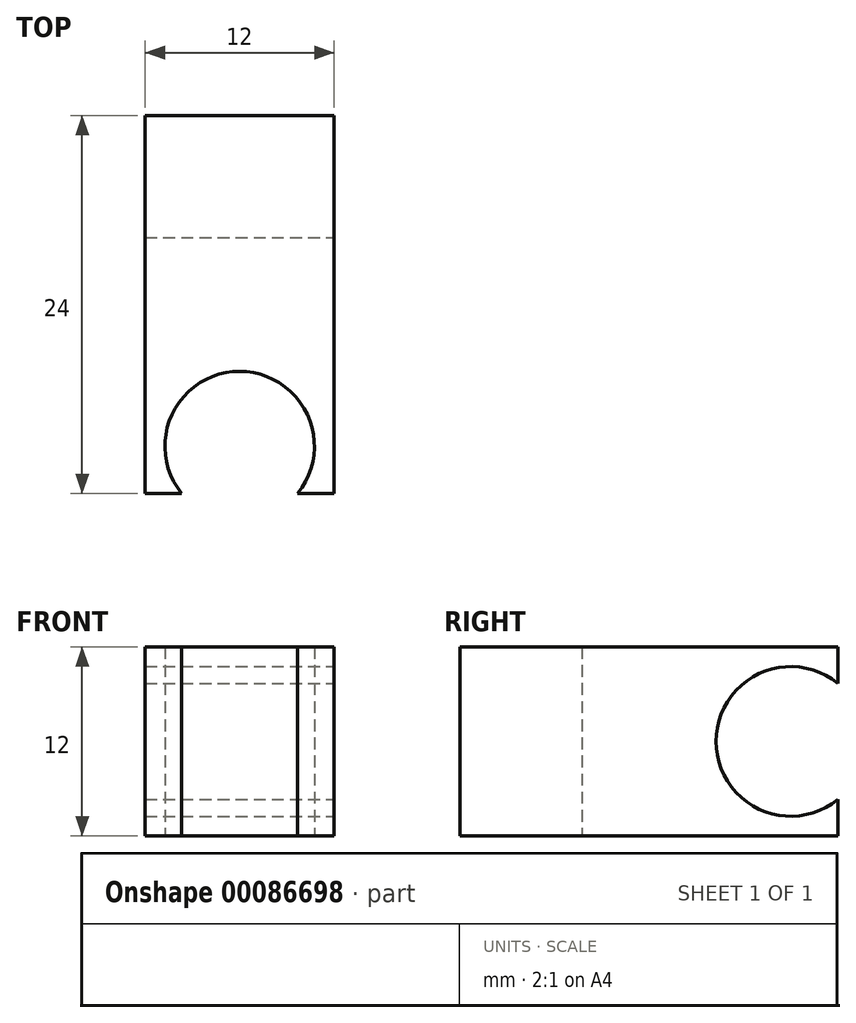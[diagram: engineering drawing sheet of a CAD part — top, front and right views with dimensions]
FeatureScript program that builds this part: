
annotation { "Feature Type Name" : "Feature", "Feature Type Description" : "" }
export const myFeature = defineFeature(function(context is Context, id is Id, definition is map)
    precondition{}
    {
        {
            var Q0;
            Q0=qCreatedBy(makeId("Top.planeOp"),FACE);
            var sketch = newSketch(context, id + "F0", { "sketchPlane" : qUnion([Q0])});
            skLineSegment(sketch, "E0.bottom", {"start": v(6, 12) * mm, "end": v(-6, 12) * mm});
            skLineSegment(sketch, "E0.top", {"start": v(6, -12) * mm, "end": v(-6, -12) * mm});
            skLineSegment(sketch, "E0.left", {"start": v(6, 12) * mm, "end": v(6, -12) * mm});
            skLineSegment(sketch, "E0.right", {"start": v(-6, 12) * mm, "end": v(-6, -12) * mm});
            skPoint(sketch, "E0.middle", {"position": v(0, 0) * mm});
            skLineSegment(sketch, "E1", {"start": v(-15.84, 0) * mm, "end": v(20.57, 0) * mm, "construction": true});
            skPoint(sketch, "E1.endSnap0", {"position": v(6, 0) * mm});
            skCircle(sketch, "E2", {"center": v(0, -9) * mm, "radius": 4.75 * mm});
            skSolve(sketch);
        }
        {
            var Q0;
            {var subQ4=sQuery(id+"F0.wireOp",EDGE,"E0.left");Q0=makeQuery(id+"F0.imprint","IMPRINT",FACE,{"disambiguationData":[TD([[makeQuery(id+"F0.imprint","IMPRINT",EDGE,{"derivedFrom":subQ4}),-1.0]])]});}
            extrude(context, id + "F1", {"entities" : qUnion([Q0]), "depth" : 12 * mm});
        }
        {
            var Q0;
            Q0=makeQuery(id+"F1.opExtrude","SWEPT_FACE",FACE,{"disambiguationData":[OSD([sQuery(id+"F0.wireOp",EDGE,"E0.left")])]});
            var sketch = newSketch(context, id + "F2", { "sketchPlane" : qUnion([Q0])});
            skCircle(sketch, "E3", {"center": v(9, 6) * mm, "radius": 4.75 * mm});
            skLineSegment(sketch, "E4", {"start": v(12, 6) * mm, "end": v(6, 6) * mm, "construction": true});
            skSolve(sketch);
        }
        {
            var Q0;
            {var subQ0=sQuery(id+"F2.wireOp",EDGE,"E3");var subQ1=makeQuery(id+"F1.opExtrude","SWEPT_EDGE",EDGE,{"disambiguationData":[OSD([sQuery(id+"F0.wireOp",EDGE,"E0.bottom"),sQuery(id+"F0.wireOp",EDGE,"E0.left")])]});var subQ2=makeQuery(id+"F2.imprint","INTERSECT",VERTEX,{"disambiguationData":[OD(0.0)],"derivedFrom":[subQ1,subQ0]});Q0=makeQuery(id+"F2.imprint","IMPRINT",FACE,{"disambiguationData":[TD([[makeQuery(id+"F2.imprint","IMPRINT",EDGE,{"disambiguationData":[TD([[subQ2,1.0]])],"derivedFrom":subQ0}),1.0]])]});}
            var Q1;
            Q1=sQuery(id+"F2.wireOp",EDGE,"E3");
            extrude(context, id + "F3", {"entities" : qUnion([Q0]), "operationType" : NewBodyOperationType.REMOVE, "surfaceEntities" : qUnion([Q1]), "endBound" : BoundingType.UP_TO_NEXT, "oppositeDirection" : true, "depth" : 25 * mm});
        }
    });
